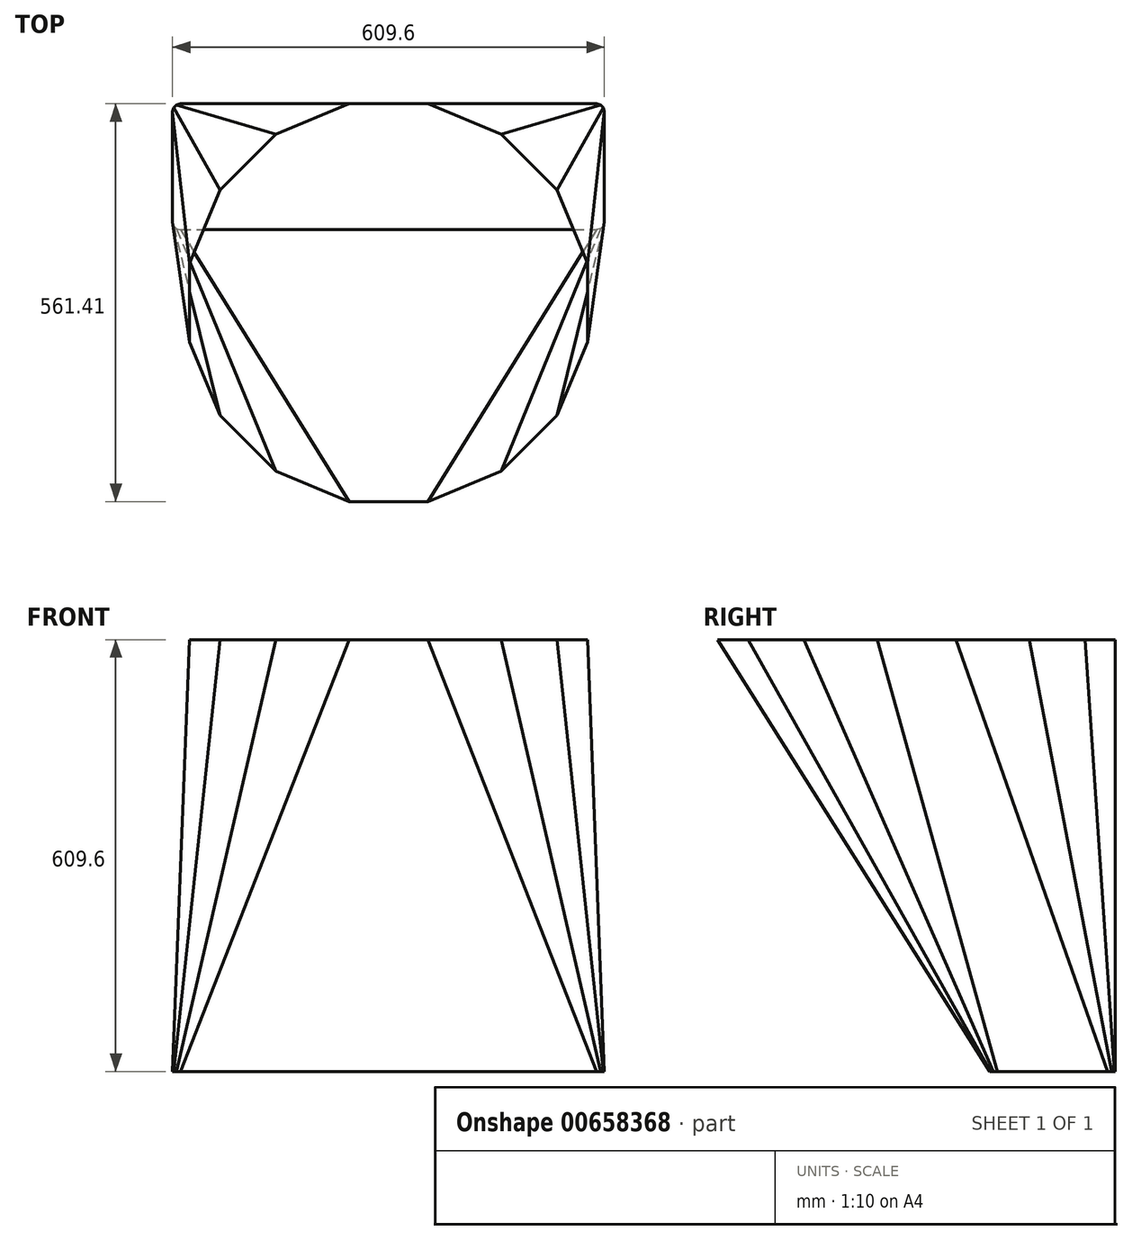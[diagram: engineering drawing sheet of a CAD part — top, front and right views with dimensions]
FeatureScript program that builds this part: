
annotation { "Feature Type Name" : "Feature", "Feature Type Description" : "" }
export const myFeature = defineFeature(function(context is Context, id is Id, definition is map)
    precondition{}
    {
        {
            var Q0;
            Q0=qCreatedBy(makeId("Top.planeOp"),FACE);
            var sketch = newSketch(context, id + "F0", { "sketchPlane" : qUnion([Q0])});
            skLineSegment(sketch, "E0.top", {"start": v(-293.92, -177.8) * mm, "end": v(293.92, -177.8) * mm});
            skLineSegment(sketch, "E0.left", {"start": v(-304.8, -10.88) * mm, "end": v(-304.8, -166.92) * mm});
            skLineSegment(sketch, "E1", {"start": v(0, -88.9) * mm, "end": v(-101.82, -88.9) * mm, "construction": true});
            skLineSegment(sketch, "E2.9", {"start": v(-304.8, -11.06) * mm, "end": v(-303.37, -5.56) * mm});
            skLineSegment(sketch, "E2.10", {"start": v(-303.37, -5.56) * mm, "end": v(-299.4, -1.51) * mm});
            skLineSegment(sketch, "E2.11", {"start": v(-299.4, -1.51) * mm, "end": v(-293.92, 0) * mm});
            skPoint(sketch, "E3.orphan", {"position": v(-304.8, 0) * mm});
            skPoint(sketch, "E4.MirrorP", {"position": v(-283.03, 0.18) * mm});
            skLineSegment(sketch, "E5.MirrorCS", {"start": v(-299.4, -176.29) * mm, "end": v(-293.92, -177.8) * mm});
            skLineSegment(sketch, "E6.MirrorCS", {"start": v(-304.8, -166.74) * mm, "end": v(-303.37, -172.24) * mm});
            skLineSegment(sketch, "E7.MirrorCS", {"start": v(-303.37, -172.24) * mm, "end": v(-299.4, -176.29) * mm});
            skPoint(sketch, "E8.MirrorP", {"position": v(-304.8, -177.8) * mm});
            skPoint(sketch, "E9.MirrorP", {"position": v(-283.03, -177.98) * mm});
            skLineSegment(sketch, "E10.MirrorCS", {"start": v(299.4, -1.51) * mm, "end": v(293.92, 0) * mm});
            skLineSegment(sketch, "E11.MirrorCS", {"start": v(299.4, -176.29) * mm, "end": v(293.92, -177.8) * mm});
            skLineSegment(sketch, "E12.MirrorCS", {"start": v(303.37, -172.24) * mm, "end": v(299.4, -176.29) * mm});
            skLineSegment(sketch, "E13.MirrorCS", {"start": v(303.37, -5.56) * mm, "end": v(299.4, -1.51) * mm});
            skLineSegment(sketch, "E14.MirrorCS", {"start": v(304.8, -166.74) * mm, "end": v(303.37, -172.24) * mm});
            skLineSegment(sketch, "E15.MirrorCS", {"start": v(304.8, -11.06) * mm, "end": v(303.37, -5.56) * mm});
            skPoint(sketch, "E16.MirrorP", {"position": v(304.8, -177.8) * mm});
            skLineSegment(sketch, "E17.MirrorCS", {"start": v(304.8, -10.88) * mm, "end": v(304.8, -166.92) * mm});
            skPoint(sketch, "E18.MirrorP", {"position": v(304.8, 0) * mm});
            skPoint(sketch, "E19.MirrorP", {"position": v(283.03, -177.98) * mm});
            skPoint(sketch, "E20.MirrorP", {"position": v(283.03, 0.18) * mm});
            skLineSegment(sketch, "E21", {"start": v(-293.92, 0) * mm, "end": v(293.92, 0) * mm});
            skSolve(sketch);
        }
        {
            var Q0;
            Q0=qCreatedBy(makeId("Top.planeOp"),FACE);
            cPlane(context, id + "F1", {"entities" : qUnion([Q0]), "cplaneType" : CPlaneType.OFFSET, "offset" : 609.6 * mm, "width" : 152.4 * mm, "height" : 152.4 * mm});
        }
        {
            var Q0;
            Q0=qCreatedBy(id+"F1.planeOp",FACE);
            var sketch = newSketch(context, id + "F2", { "sketchPlane" : qUnion([Q0])});
            skCircle(sketch, "E22.cCircle", {"center": v(0, -280.7) * mm, "radius": 280.7 * mm, "construction": true});
            skLineSegment(sketch, "E22.0", {"start": v(-55.84, 0) * mm, "end": v(55.84, 0) * mm});
            skLineSegment(sketch, "E22.1", {"start": v(55.84, 0) * mm, "end": v(159, -42.74) * mm});
            skLineSegment(sketch, "E22.2", {"start": v(159, -42.74) * mm, "end": v(237.97, -121.7) * mm});
            skLineSegment(sketch, "E22.3", {"start": v(237.97, -121.7) * mm, "end": v(280.7, -224.87) * mm});
            skLineSegment(sketch, "E22.4", {"start": v(280.7, -224.87) * mm, "end": v(280.7, -336.54) * mm});
            skLineSegment(sketch, "E22.5", {"start": v(280.7, -336.54) * mm, "end": v(237.97, -439.71) * mm});
            skLineSegment(sketch, "E22.6", {"start": v(237.97, -439.71) * mm, "end": v(159, -518.68) * mm});
            skLineSegment(sketch, "E22.7", {"start": v(159, -518.68) * mm, "end": v(55.84, -561.41) * mm});
            skLineSegment(sketch, "E22.8", {"start": v(55.84, -561.41) * mm, "end": v(-55.84, -561.41) * mm});
            skLineSegment(sketch, "E22.9", {"start": v(-55.84, -561.41) * mm, "end": v(-159, -518.68) * mm});
            skLineSegment(sketch, "E22.10", {"start": v(-159, -518.68) * mm, "end": v(-237.97, -439.71) * mm});
            skLineSegment(sketch, "E22.11", {"start": v(-237.97, -439.71) * mm, "end": v(-280.7, -336.54) * mm});
            skLineSegment(sketch, "E22.12", {"start": v(-280.7, -336.54) * mm, "end": v(-280.7, -224.87) * mm});
            skLineSegment(sketch, "E22.13", {"start": v(-280.7, -224.87) * mm, "end": v(-237.97, -121.7) * mm});
            skLineSegment(sketch, "E22.14", {"start": v(-237.97, -121.7) * mm, "end": v(-159, -42.74) * mm});
            skLineSegment(sketch, "E22.15", {"start": v(-159, -42.74) * mm, "end": v(-55.84, 0) * mm});
            skPoint(sketch, "E22.0.midPoint", {"position": v(0, 0) * mm});
            skSolve(sketch);
        }
        {
            var Q0;
            Q0=makeQuery(id+"F0.imprint","IMPRINT",FACE,{"disambiguationData":[TD([[makeQuery(id+"F0.imprint","IMPRINT",EDGE,{"derivedFrom":sQuery(id+"F0.wireOp",EDGE,"E0.top")}),1.0]])]});
            var Q1;
            Q1=makeQuery(id+"F2.imprint","IMPRINT",FACE,{"disambiguationData":[TD([[makeQuery(id+"F2.imprint","IMPRINT",EDGE,{"derivedFrom":sQuery(id+"F2.wireOp",EDGE,"E22.0")}),-1.0]])]});
            var Q2;
            Q2=makeQuery(id+"F0.imprint","IMPRINT",FACE,{"disambiguationData":[TD([[makeQuery(id+"F0.imprint","IMPRINT",EDGE,{"derivedFrom":sQuery(id+"F0.wireOp",EDGE,"E0.top")}),1.0]])]});
            var Q3;
            Q3=makeQuery(id+"F2.imprint","IMPRINT",FACE,{"disambiguationData":[TD([[makeQuery(id+"F2.imprint","IMPRINT",EDGE,{"derivedFrom":sQuery(id+"F2.wireOp",EDGE,"E22.0")}),-1.0]])]});
            loft(context, id + "F3", {"bodyType" : ToolBodyType.SURFACE, "sheetProfilesArray" : [{ "sheetProfileEntities" : qUnion([Q0]) }, { "sheetProfileEntities" : qUnion([Q1]) }], "wireProfilesArray" : [{ "wireProfileEntities" : qUnion([Q2]) }, { "wireProfileEntities" : qUnion([Q3]) }]});
        }
    });
